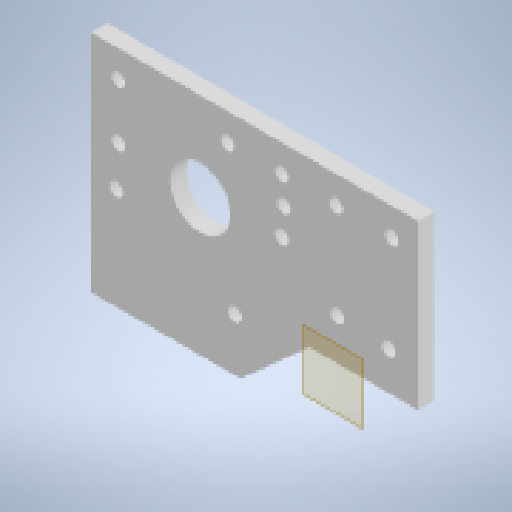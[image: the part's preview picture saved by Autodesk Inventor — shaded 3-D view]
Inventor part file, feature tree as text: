
AUTODESK INVENTOR PART (.ipt)
format: ipt  version: 2023.2 (Build 272271000, 271)  size: 367,104 bytes
history: native  units: mm
features: reference x13, other x4, sketch x3, hole x3, extrude x1, plane x1
ambient origin geometry x8: Origin, YZ Plane, XZ Plane, XY Plane, X Axis, Y Axis, Z Axis, Center Point
bodies: Body1 (feature_tree)
feature tree (25):
  sketch  "Sketch1"  dims[d0=120.0mm d1=40.0mm]
  extrude  "Extrusion2"  Depth=120.0mm
  plane  "Work Plane1"
  hole  "Hole2"  [1 undecoded]
  hole  "Hole3"  [1 undecoded]
  hole  "Hole4"  [1 undecoded]
  reference  "Reference1"
  reference  "Reference2"
  reference  "Reference3"
  reference  "Reference4"
  reference  "Reference5"
  reference  "Reference6"
  reference  "Reference7"
  reference  "Reference8"
  reference  "Reference9"
  reference  "Reference10"
  reference  "Reference11"
  reference  "Reference12"
  sketch  "Sketch2"  dims[d5=20.0mm d36=22.2mm]
  reference  "Reference13"
  sketch  "Sketch3"  dims[d37=32.5mm d41=47.0mm d42=47.0mm d43=9.2mm d44=9.2mm d45=15.0mm d47=50.0mm d48=50.0mm d49=6.0mm d50=0.0mm d58=5.1mm d59=6.0mm d60=9.2mm d61=3.0mm d62=90.0deg d63=8.0mm d64=20.594885mm d65=5.1mm d66=6.0mm d67=9.2mm d68=3.0mm d69=90.0deg d70=8.0mm d71=20.594885mm d72=5.1mm d73=6.0mm d74=9.2mm d75=3.0mm d76=90.0deg d77=8.0mm d78=20.594885mm d79=15.0mm]
  parser-record x1  (decoder bookkeeping rows leaked as tree rows — omitted from the tree; the rows remain in map.json)
  other  "Main Assembly.iam"
  other  "C beam extrusion 250:1"
  other  "Y axis motor mount:1"
note: 3 required parameter values undecoded (feature->parameter linkage not recoverable at this tier; creation-order binding heuristic only, values carry confidence <= 0.55)
note: 1 file-system path scrubbed to <path> (originals preserved in map.json)
